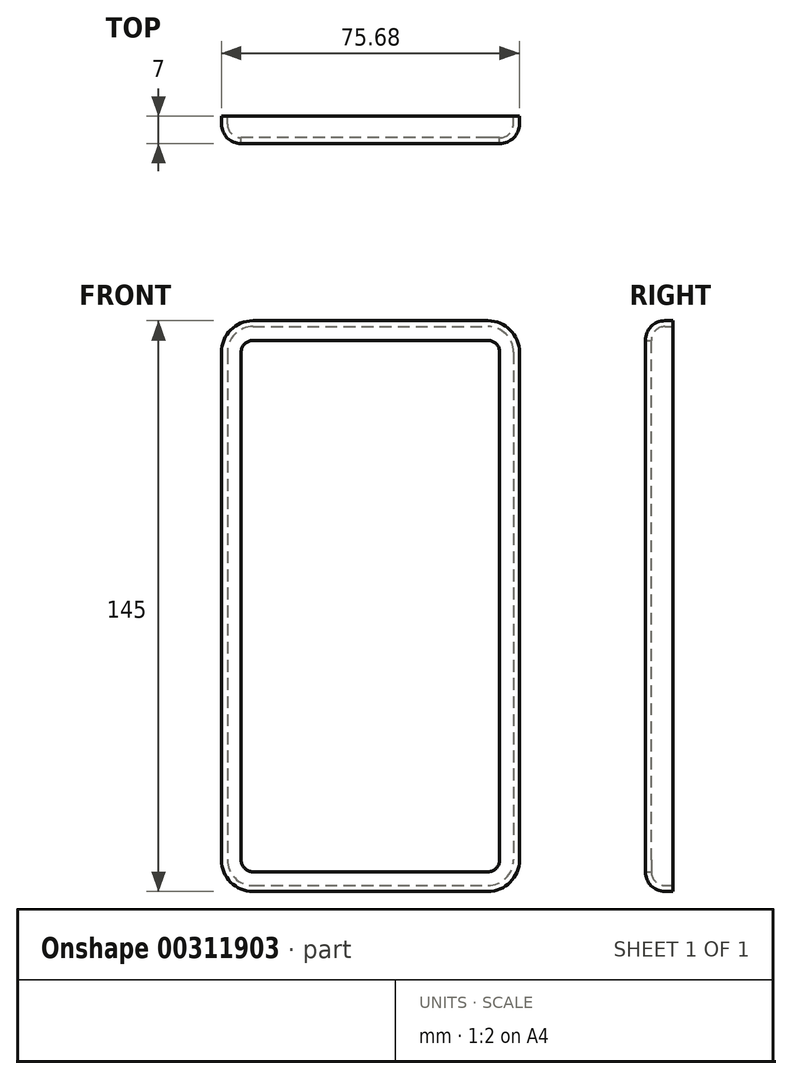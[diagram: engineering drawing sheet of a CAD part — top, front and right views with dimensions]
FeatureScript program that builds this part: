
annotation { "Feature Type Name" : "Feature", "Feature Type Description" : "" }
export const myFeature = defineFeature(function(context is Context, id is Id, definition is map)
    precondition{}
    {
        {
            var Q0;
            Q0=qCreatedBy(makeId("Front.planeOp"),FACE);
            var sketch = newSketch(context, id + "F0", { "sketchPlane" : qUnion([Q0])});
            skLineSegment(sketch, "E0.bottom", {"start": v(-28.84, 71.77) * mm, "end": v(28.84, 71.77) * mm});
            skLineSegment(sketch, "E0.top", {"start": v(-28.84, -71.77) * mm, "end": v(28.84, -71.77) * mm});
            skLineSegment(sketch, "E0.left", {"start": v(-36.85, 63.76) * mm, "end": v(-36.85, -63.76) * mm});
            skLineSegment(sketch, "E0.right", {"start": v(36.85, 63.76) * mm, "end": v(36.85, -63.76) * mm});
            skPoint(sketch, "E1.visualSharp", {"position": v(-36.84, 71.77) * mm});
            skArc(sketch, "E1.filletArc", {"start": v(-28.84, 71.77) * mm, "mid": v(-34.5, 69.42) * mm, "end": v(-36.85, 63.76) * mm});
            skPoint(sketch, "E2.visualSharp", {"position": v(36.84, 71.77) * mm});
            skArc(sketch, "E2.filletArc", {"start": v(36.85, 63.76) * mm, "mid": v(34.5, 69.42) * mm, "end": v(28.84, 71.77) * mm});
            skPoint(sketch, "E3.visualSharp", {"position": v(-36.84, -71.77) * mm});
            skArc(sketch, "E3.filletArc", {"start": v(-36.85, -63.76) * mm, "mid": v(-34.5, -69.42) * mm, "end": v(-28.84, -71.77) * mm});
            skPoint(sketch, "E4.visualSharp", {"position": v(36.84, -71.77) * mm});
            skArc(sketch, "E4.filletArc", {"start": v(28.84, -71.77) * mm, "mid": v(34.5, -69.42) * mm, "end": v(36.85, -63.76) * mm});
            skLineSegment(sketch, "E5.bottom", {"start": v(-29.84, 72.5) * mm, "end": v(29.84, 72.5) * mm});
            skLineSegment(sketch, "E5.top", {"start": v(-29.84, -72.5) * mm, "end": v(29.84, -72.5) * mm});
            skLineSegment(sketch, "E5.left", {"start": v(-37.84, 64.5) * mm, "end": v(-37.84, -64.5) * mm});
            skLineSegment(sketch, "E5.right", {"start": v(37.84, 64.5) * mm, "end": v(37.84, -64.5) * mm});
            skPoint(sketch, "E6.visualSharp", {"position": v(-37.84, 72.5) * mm});
            skArc(sketch, "E6.filletArc", {"start": v(-29.84, 72.5) * mm, "mid": v(-35.5, 70.16) * mm, "end": v(-37.84, 64.5) * mm});
            skPoint(sketch, "E7.visualSharp", {"position": v(37.84, 72.5) * mm});
            skArc(sketch, "E7.filletArc", {"start": v(37.84, 64.5) * mm, "mid": v(35.5, 70.16) * mm, "end": v(29.84, 72.5) * mm});
            skPoint(sketch, "E8.visualSharp", {"position": v(-37.84, -72.5) * mm});
            skArc(sketch, "E8.filletArc", {"start": v(-37.84, -64.5) * mm, "mid": v(-35.5, -70.16) * mm, "end": v(-29.84, -72.5) * mm});
            skPoint(sketch, "E9.visualSharp", {"position": v(37.84, -72.5) * mm});
            skArc(sketch, "E9.filletArc", {"start": v(29.84, -72.5) * mm, "mid": v(35.5, -70.16) * mm, "end": v(37.84, -64.5) * mm});
            skSolve(sketch);
        }
        {
            var Q0;
            Q0=makeQuery(id+"F0.imprint","IMPRINT",FACE,{"disambiguationData":[TD([[makeQuery(id+"F0.imprint","IMPRINT",EDGE,{"derivedFrom":sQuery(id+"F0.wireOp",EDGE,"E0.bottom")}),-1.0]])]});
            extrude(context, id + "F1", {"entities" : qUnion([Q0]), "depth" : (13.78 - 8.67) * mm});
        }
        {
            var Q0;
            Q0=makeQuery(id+"F1.opExtrude","CAP_EDGE",EDGE,{"disambiguationData":[OSD([sQuery(id+"F0.wireOp",EDGE,"E0.right")])],"isStart":false});
            fillet(context, id + "F2", {"entities" : qUnion([Q0]), "radius" : 5 * mm, "tangentPropagation" : true, "allowEdgeOverflow" : false});
        }
        {
            var Q0;
            Q0=makeQuery(id+"F0.imprint","IMPRINT",FACE,{"disambiguationData":[TD([[makeQuery(id+"F0.imprint","IMPRINT",EDGE,{"derivedFrom":sQuery(id+"F0.wireOp",EDGE,"E0.bottom")}),1.0]])]});
            var Q1;
            Q1=makeQuery(id+"F0.imprint","IMPRINT",FACE,{"disambiguationData":[TD([[makeQuery(id+"F0.imprint","IMPRINT",EDGE,{"derivedFrom":sQuery(id+"F0.wireOp",EDGE,"E0.bottom")}),-1.0]])]});
            extrude(context, id + "F3", {"entities" : qUnion([Q0, Q1]), "operationType" : NewBodyOperationType.ADD, "depth" : 7 * mm});
        }
        {
            var Q0;
            Q0=makeQuery(id+"F3.opExtrude","CAP_EDGE",EDGE,{"disambiguationData":[OSD([sQuery(id+"F0.wireOp",EDGE,"E5.right")])],"isStart":false});
            fillet(context, id + "F4", {"entities" : qUnion([Q0]), "radius" : 5 * mm, "tangentPropagation" : true, "allowEdgeOverflow" : false});
        }
        {
            var Q0;
            Q0=makeQuery(id+"F3.boolean.opBoolean","MERGE",FACE,{"derivedFrom":[makeQuery(id+"F1.opExtrude","CAP_FACE",FACE,{"disambiguationData":[OSD([sQuery(id+"F0.wireOp",EDGE,"E0.bottom"),sQuery(id+"F0.wireOp",EDGE,"E0.top"),sQuery(id+"F0.wireOp",EDGE,"E0.left"),sQuery(id+"F0.wireOp",EDGE,"E0.right"),sQuery(id+"F0.wireOp",EDGE,"E1.filletArc"),sQuery(id+"F0.wireOp",EDGE,"E2.filletArc"),sQuery(id+"F0.wireOp",EDGE,"E3.filletArc"),sQuery(id+"F0.wireOp",EDGE,"E4.filletArc")])],"isStart":true}),makeQuery(id+"F3.opExtrude","CAP_FACE",FACE,{"disambiguationData":[OSD([sQuery(id+"F0.wireOp",EDGE,"E5.bottom"),sQuery(id+"F0.wireOp",EDGE,"E5.top"),sQuery(id+"F0.wireOp",EDGE,"E5.left"),sQuery(id+"F0.wireOp",EDGE,"E5.right"),sQuery(id+"F0.wireOp",EDGE,"E6.filletArc"),sQuery(id+"F0.wireOp",EDGE,"E7.filletArc"),sQuery(id+"F0.wireOp",EDGE,"E8.filletArc"),sQuery(id+"F0.wireOp",EDGE,"E9.filletArc")])],"isStart":true})]});
            var Q1;
            Q1=makeQuery(id+"F3.opExtrude","CAP_FACE",FACE,{"disambiguationData":[OSD([sQuery(id+"F0.wireOp",EDGE,"E5.bottom"),sQuery(id+"F0.wireOp",EDGE,"E5.top"),sQuery(id+"F0.wireOp",EDGE,"E5.left"),sQuery(id+"F0.wireOp",EDGE,"E5.right"),sQuery(id+"F0.wireOp",EDGE,"E6.filletArc"),sQuery(id+"F0.wireOp",EDGE,"E7.filletArc"),sQuery(id+"F0.wireOp",EDGE,"E8.filletArc"),sQuery(id+"F0.wireOp",EDGE,"E9.filletArc")])],"isStart":false});
            shell(context, id + "F5", {"entities" : qUnion([Q0, Q1]), "thickness" : 1.5 * mm});
        }
    });
